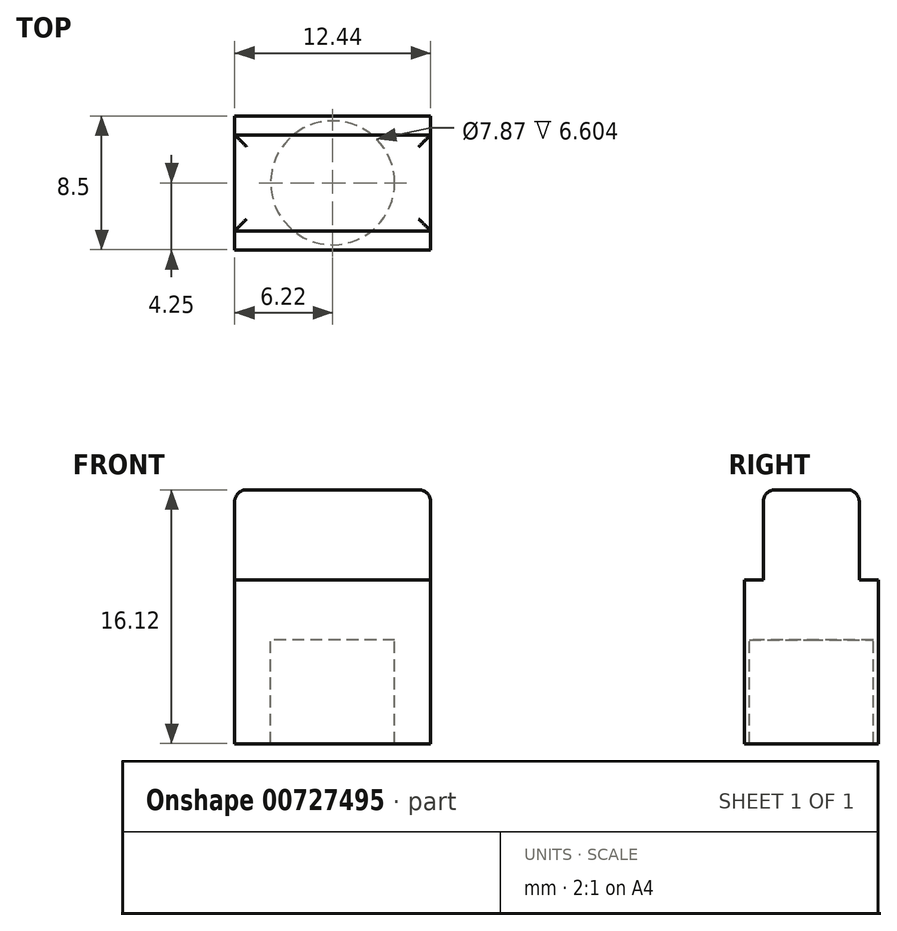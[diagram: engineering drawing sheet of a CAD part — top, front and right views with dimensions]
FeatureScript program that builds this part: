
annotation { "Feature Type Name" : "Feature", "Feature Type Description" : "" }
export const myFeature = defineFeature(function(context is Context, id is Id, definition is map)
    precondition{}
    {
        {
            var Q0;
            Q0=qCreatedBy(makeId("Top.planeOp"),FACE);
            var sketch = newSketch(context, id + "F0", { "sketchPlane" : qUnion([Q0])});
            skLineSegment(sketch, "E0.bottom", {"start": v(6.22, 3.05) * mm, "end": v(-6.22, 3.05) * mm});
            skLineSegment(sketch, "E0.top", {"start": v(6.22, -3.05) * mm, "end": v(-6.22, -3.05) * mm});
            skLineSegment(sketch, "E0.left", {"start": v(6.22, 3.05) * mm, "end": v(6.22, -3.05) * mm});
            skLineSegment(sketch, "E0.right", {"start": v(-6.22, 3.05) * mm, "end": v(-6.22, -3.05) * mm});
            skPoint(sketch, "E0.middle", {"position": v(0, 0) * mm});
            skSolve(sketch);
        }
        {
            var Q0;
            Q0=makeQuery(id+"F0.imprint","IMPRINT",FACE,{"disambiguationData":[TD([[makeQuery(id+"F0.imprint","IMPRINT",EDGE,{"derivedFrom":sQuery(id+"F0.wireOp",EDGE,"E0.bottom")}),1.0]])]});
            extrude(context, id + "F1", {"entities" : qUnion([Q0]), "depth" : 5.7 * mm, "offsetDistance" : 25.4 * mm});
        }
        {
            var Q0;
            Q0=qCreatedBy(makeId("Top.planeOp"),FACE);
            var sketch = newSketch(context, id + "F2", { "sketchPlane" : qUnion([Q0])});
            skLineSegment(sketch, "E1.bottom", {"start": v(6.22, -4.25) * mm, "end": v(-6.22, -4.25) * mm});
            skLineSegment(sketch, "E1.top", {"start": v(6.22, 4.25) * mm, "end": v(-6.22, 4.25) * mm});
            skLineSegment(sketch, "E1.left", {"start": v(6.22, -4.25) * mm, "end": v(6.22, 4.25) * mm});
            skLineSegment(sketch, "E1.right", {"start": v(-6.22, -4.25) * mm, "end": v(-6.22, 4.25) * mm});
            skPoint(sketch, "E1.middle", {"position": v(0, 0) * mm});
            skSolve(sketch);
        }
        {
            var Q0;
            Q0=makeQuery(id+"F2.imprint","IMPRINT",FACE,{"disambiguationData":[TD([[makeQuery(id+"F2.imprint","IMPRINT",EDGE,{"derivedFrom":sQuery(id+"F2.wireOp",EDGE,"E1.bottom")}),-1.0]])]});
            extrude(context, id + "F3", {"entities" : qUnion([Q0]), "operationType" : NewBodyOperationType.ADD, "oppositeDirection" : true, "depth" : 10.4 * mm, "offsetDistance" : 25.4 * mm});
        }
        {
            var Q0;
            Q0=makeQuery(id+"F1.opExtrude","CAP_FACE",FACE,{"disambiguationData":[OSD([sQuery(id+"F0.wireOp",EDGE,"E0.bottom"),sQuery(id+"F0.wireOp",EDGE,"E0.top"),sQuery(id+"F0.wireOp",EDGE,"E0.left"),sQuery(id+"F0.wireOp",EDGE,"E0.right")])],"isStart":false});
            fillet(context, id + "F4", {"entities" : qUnion([Q0]), "radius" : 0.76 * mm, "tangentPropagation" : true, "allowEdgeOverflow" : false});
        }
        {
            var Q0;
            Q0=qCreatedBy(makeId("Top.planeOp"),FACE);
            cPlane(context, id + "F5", {"entities" : qUnion([Q0]), "cplaneType" : CPlaneType.OFFSET, "offset" : 3.8 * mm, "oppositeDirection" : true, "width" : 152.4 * mm, "height" : 152.4 * mm});
        }
        {
            var Q0;
            Q0=qCreatedBy(id+"F5.planeOp",FACE);
            var sketch = newSketch(context, id + "F6", { "sketchPlane" : qUnion([Q0])});
            skPoint(sketch, "E2", {"position": v(0, 0) * mm});
            skSolve(sketch);
        }
        {
            var Q0;
            Q0=sQuery(id+"F6.wireOp",VERTEX,"E2");
            var Q1;
            Q1=makeQuery(id+"F1.opExtrude","SWEPT_BODY",BODY,{"disambiguationData":[OSD([sQuery(id+"F0.wireOp",EDGE,"E0.bottom"),sQuery(id+"F0.wireOp",EDGE,"E0.top"),sQuery(id+"F0.wireOp",EDGE,"E0.left"),sQuery(id+"F0.wireOp",EDGE,"E0.right")])]});
            hole(context, id + "F7", {"style" : HoleStyle.SIMPLE, "endStyle" : HoleEndStyle.THROUGH, "holeDiameter" : 7.87 * mm, "majorDiameter" : 6.35 * mm, "isTappedThrough" : true, "tappedDepth" : 12.7 * mm, "tapClearance" : 3, "locations" : qUnion([Q0]), "scope" : qUnion([Q1])});
        }
    });
